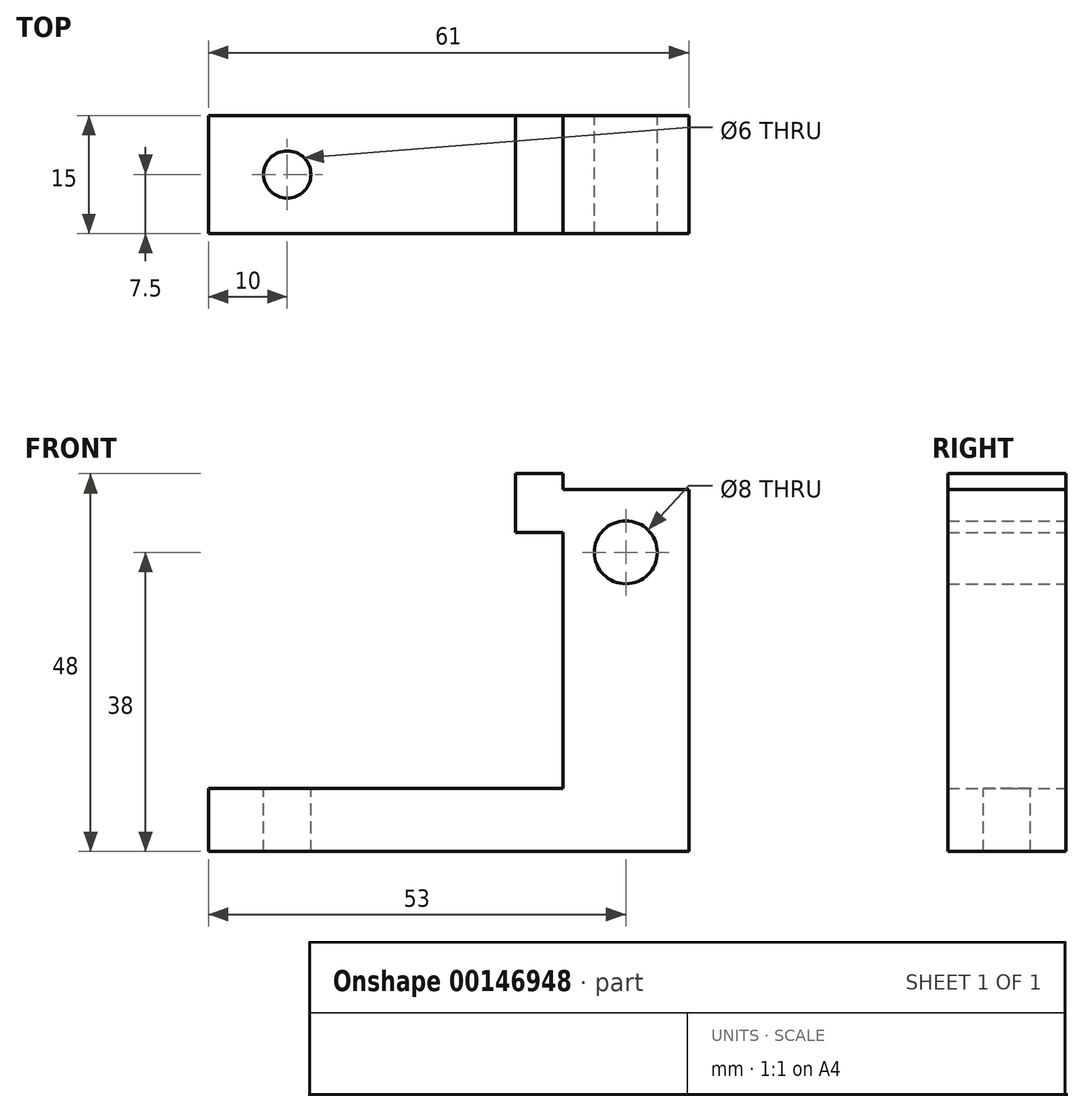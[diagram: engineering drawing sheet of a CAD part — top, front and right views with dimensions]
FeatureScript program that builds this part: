
annotation { "Feature Type Name" : "Feature", "Feature Type Description" : "" }
export const myFeature = defineFeature(function(context is Context, id is Id, definition is map)
    precondition{}
    {
        {
            var Q0;
            Q0=qCreatedBy(makeId("Front.planeOp"),FACE);
            var sketch = newSketch(context, id + "F0", { "sketchPlane" : qUnion([Q0])});
            skLineSegment(sketch, "E0.bottom", {"start": v(0, 0) * mm, "end": v(45, 0) * mm});
            skLineSegment(sketch, "E0.top", {"start": v(0, 8) * mm, "end": v(61, 8) * mm});
            skLineSegment(sketch, "E0.left", {"start": v(0, 0) * mm, "end": v(0, 8) * mm});
            skLineSegment(sketch, "E1.bottom", {"start": v(45, 8) * mm, "end": v(45, 8) * mm});
            skLineSegment(sketch, "E1.top", {"start": v(45, 46) * mm, "end": v(61, 46) * mm});
            skLineSegment(sketch, "E1.left", {"start": v(45, 8) * mm, "end": v(45, 46) * mm});
            skLineSegment(sketch, "E1.right", {"start": v(61, 8) * mm, "end": v(61, 46) * mm});
            skLineSegment(sketch, "E2", {"start": v(53, 48) * mm, "end": v(53, 8) * mm, "construction": true});
            skCircle(sketch, "E3", {"center": v(53, 38) * mm, "radius": 4 * mm});
            skLineSegment(sketch, "E4", {"start": v(61, 8) * mm, "end": v(61, 0) * mm});
            skLineSegment(sketch, "E5.bottom", {"start": v(61, 46) * mm, "end": v(45, 46) * mm});
            skLineSegment(sketch, "E5.top", {"start": v(61, 48) * mm, "end": v(45, 48) * mm});
            skLineSegment(sketch, "E5.left", {"start": v(61, 46) * mm, "end": v(61, 48) * mm});
            skPoint(sketch, "E6.end.orphan", {"position": v(45, 0) * mm});
            skLineSegment(sketch, "E7", {"start": v(45, 8) * mm, "end": v(45, 0) * mm});
            skLineSegment(sketch, "E8", {"start": v(45, 0) * mm, "end": v(61, 0) * mm});
            skLineSegment(sketch, "E9", {"start": v(45, 8) * mm, "end": v(61, 8) * mm});
            skLineSegment(sketch, "E10", {"start": v(45, 46) * mm, "end": v(45, 48) * mm});
            skLineSegment(sketch, "E11.bottom", {"start": v(45, 40.5) * mm, "end": v(39, 40.5) * mm});
            skLineSegment(sketch, "E11.top", {"start": v(45, 48) * mm, "end": v(39, 48) * mm});
            skLineSegment(sketch, "E11.left", {"start": v(45, 40.5) * mm, "end": v(45, 48) * mm});
            skLineSegment(sketch, "E11.right", {"start": v(39, 40.5) * mm, "end": v(39, 48) * mm});
            skSolve(sketch);
        }
        {
            var Q0;
            Q0=makeQuery(id+"F0.imprint","IMPRINT",FACE,{"disambiguationData":[TD([[makeQuery(id+"F0.imprint","IMPRINT",EDGE,{"derivedFrom":sQuery(id+"F0.wireOp",EDGE,"E0.bottom")}),1.0]])]});
            var Q1;
            Q1=makeQuery(id+"F0.imprint","IMPRINT",FACE,{"disambiguationData":[TD([[makeQuery(id+"F0.imprint","IMPRINT",EDGE,{"derivedFrom":sQuery(id+"F0.wireOp",EDGE,"E1.bottom")}),1.0]])]});
            var Q2;
            Q2=makeQuery(id+"F0.imprint","IMPRINT",FACE,{"disambiguationData":[TD([[makeQuery(id+"F0.imprint","IMPRINT",EDGE,{"derivedFrom":sQuery(id+"F0.wireOp",EDGE,"E4")}),-1.0]])]});
            var Q3;
            Q3=makeQuery(id+"F0.imprint","IMPRINT",FACE,{"disambiguationData":[TD([[makeQuery(id+"F0.imprint","IMPRINT",EDGE,{"derivedFrom":sQuery(id+"F0.wireOp",EDGE,"E1.left")}),-1.0]])]});
            var Q4;
            Q4=makeQuery(id+"F0.imprint","IMPRINT",FACE,{"disambiguationData":[TD([[makeQuery(id+"F0.imprint","IMPRINT",EDGE,{"derivedFrom":sQuery(id+"F0.wireOp",EDGE,"E5.bottom")}),-1.0]])]});
            var Q5;
            {var subQ0=sQuery(id+"F0.wireOp",EDGE,"E10");Q5=makeQuery(id+"F0.imprint","IMPRINT",FACE,{"disambiguationData":[TD([[makeQuery(id+"F0.imprint","IMPRINT",EDGE,{"derivedFrom":subQ0}),1.0]])]});}
            var Q6;
            {var subQ3=sQuery(id+"F0.wireOp",EDGE,"E11.bottom");Q6=makeQuery(id+"F0.imprint","IMPRINT",FACE,{"disambiguationData":[TD([[makeQuery(id+"F0.imprint","IMPRINT",EDGE,{"derivedFrom":subQ3}),-1.0]])]});}
            extrude(context, id + "F1", {"entities" : qUnion([Q0, Q1, Q2, Q3, Q4, Q5, Q6]), "depth" : 15 * mm, "offsetDistance" : 25 * mm});
        }
        {
            var Q0;
            {var subQ0=sQuery(id+"F0.wireOp",EDGE,"E0.top");Q0=makeQuery(id+"F1.opExtrude","SWEPT_FACE",FACE,{"disambiguationData":[OSD([subQ0]),TDD([makeQuery(id+"F0.imprint","IMPRINT",EDGE,{"disambiguationData":[TD([[makeQuery(id+"F0.imprint","INTERSECT",VERTEX,{"derivedFrom":[subQ0,sQuery(id+"F0.wireOp",EDGE,"E0.left")]}),-1.0]])],"derivedFrom":subQ0})])]});}
            var sketch = newSketch(context, id + "F2", { "sketchPlane" : qUnion([Q0])});
            skLineSegment(sketch, "E12", {"start": v(0, -7.5) * mm, "end": v(0, -7.5) * mm});
            skCircle(sketch, "E13", {"center": v(10, -7.5) * mm, "radius": 3 * mm});
            skSolve(sketch);
        }
        {
            var Q0;
            Q0=makeQuery(id+"F2.imprint","IMPRINT",FACE,{"disambiguationData":[TD([[makeQuery(id+"F2.imprint","IMPRINT",EDGE,{"derivedFrom":sQuery(id+"F2.wireOp",EDGE,"E13")}),1.0]])]});
            var Q1;
            Q1=makeQuery(id+"F2.imprint","IMPRINT",FACE,{"disambiguationData":[TD([[makeQuery(id+"F2.imprint","IMPRINT",EDGE,{"derivedFrom":sQuery(id+"F2.wireOp",EDGE,"E13")}),1.0]])]});
            extrude(context, id + "F3", {"entities" : qUnion([Q0, Q1]), "operationType" : NewBodyOperationType.REMOVE, "endBound" : BoundingType.SYMMETRIC, "oppositeDirection" : true, "depth" : 111 * mm});
        }
    });
